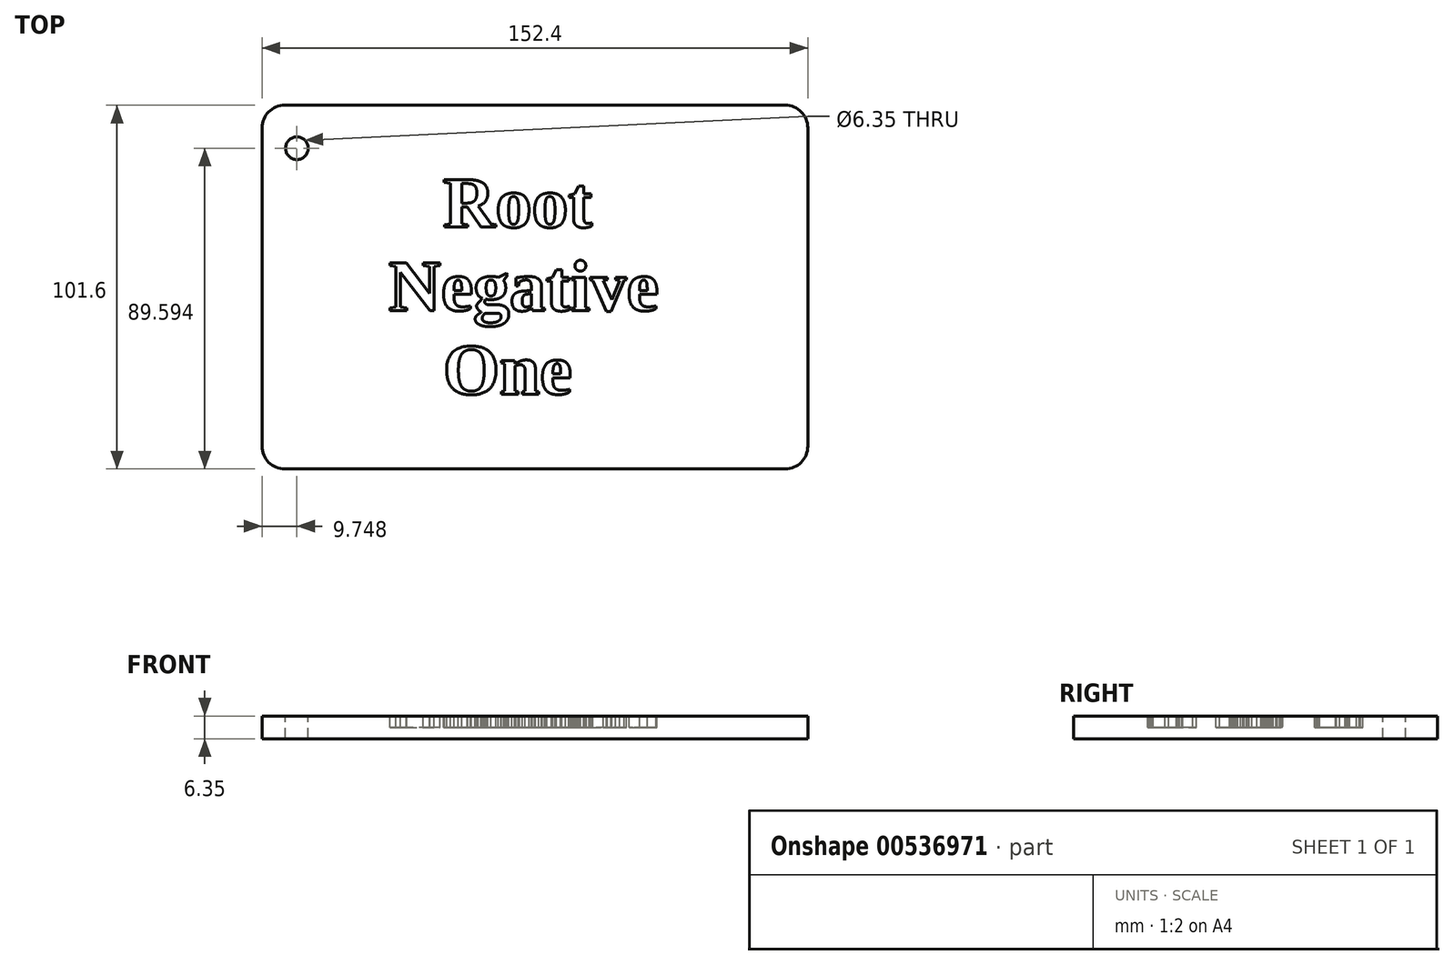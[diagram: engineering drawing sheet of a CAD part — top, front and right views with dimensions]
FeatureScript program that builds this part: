
annotation { "Feature Type Name" : "Feature", "Feature Type Description" : "" }
export const myFeature = defineFeature(function(context is Context, id is Id, definition is map)
    precondition{}
    {
        {
            var Q0;
            Q0=qCreatedBy(makeId("Top.planeOp"),FACE);
            var sketch = newSketch(context, id + "F0", { "sketchPlane" : qUnion([Q0])});
            skLineSegment(sketch, "E0.bottom", {"start": v(-67.09, 43.12) * mm, "end": v(72.61, 43.12) * mm});
            skLineSegment(sketch, "E0.top", {"start": v(-67.09, -58.48) * mm, "end": v(72.61, -58.48) * mm});
            skLineSegment(sketch, "E0.left", {"start": v(-73.44, 36.77) * mm, "end": v(-73.44, -52.13) * mm});
            skLineSegment(sketch, "E0.right", {"start": v(78.96, 36.77) * mm, "end": v(78.96, -52.13) * mm});
            skPoint(sketch, "E1.visualSharp", {"position": v(78.96, 43.12) * mm});
            skArc(sketch, "E1.filletArc", {"start": v(78.96, 36.77) * mm, "mid": v(77.1, 41.26) * mm, "end": v(72.61, 43.12) * mm});
            skPoint(sketch, "E2.visualSharp", {"position": v(78.96, -58.48) * mm});
            skArc(sketch, "E2.filletArc", {"start": v(72.61, -58.48) * mm, "mid": v(77.1, -56.62) * mm, "end": v(78.96, -52.13) * mm});
            skPoint(sketch, "E3.visualSharp", {"position": v(-73.44, -58.48) * mm});
            skArc(sketch, "E3.filletArc", {"start": v(-73.44, -52.13) * mm, "mid": v(-71.58, -56.62) * mm, "end": v(-67.09, -58.48) * mm});
            skPoint(sketch, "E4.visualSharp", {"position": v(-73.44, 43.12) * mm});
            skArc(sketch, "E4.filletArc", {"start": v(-67.09, 43.12) * mm, "mid": v(-71.58, 41.26) * mm, "end": v(-73.44, 36.77) * mm});
            skSolve(sketch);
        }
        {
            var Q0;
            Q0=makeQuery(id+"F0.imprint","IMPRINT",FACE,{"disambiguationData":[TD([[makeQuery(id+"F0.imprint","IMPRINT",EDGE,{"derivedFrom":sQuery(id+"F0.wireOp",EDGE,"E0.bottom")}),-1.0]])]});
            extrude(context, id + "F1", {"entities" : qUnion([Q0]), "depth" : 6.35 * mm, "offsetDistance" : 25.4 * mm});
        }
        {
            var Q0;
            Q0=makeQuery(id+"F1.opExtrude","CAP_FACE",FACE,{"disambiguationData":[OSD([sQuery(id+"F0.wireOp",EDGE,"E0.bottom"),sQuery(id+"F0.wireOp",EDGE,"E0.top"),sQuery(id+"F0.wireOp",EDGE,"E0.left"),sQuery(id+"F0.wireOp",EDGE,"E0.right")])],"isStart":false});
            var sketch = newSketch(context, id + "F2", { "sketchPlane" : qUnion([Q0])});
            skText(sketch, "E5", { "text": "   Root\nNegative\n   One", "fontName": "Tinos-Bold.ttf"});
            const initialGuessF2  = {"E5": [-0.0381, 0.00907, 1, 0, 0.0146]};
            skSetInitialGuess(sketch, initialGuessF2);
            skSolve(sketch);
        }
        {
            var Q0;
            Q0 = qSketchRegion(id + "F2", true);
            extrude(context, id + "F3", {"entities" : qUnion([Q0]), "operationType" : NewBodyOperationType.REMOVE, "oppositeDirection" : true, "depth" : 3.17 * mm, "offsetDistance" : 25.4 * mm});
        }
        {
            var Q0;
            {var subQ0=sQuery(id+"F0.wireOp",EDGE,"E0.left");var subQ1=sQuery(id+"F0.wireOp",EDGE,"E4.filletArc");var subQ2=sQuery(id+"F0.wireOp",EDGE,"E3.filletArc");var subQ3=sQuery(id+"F0.wireOp",EDGE,"E2.filletArc");var subQ4=sQuery(id+"F0.wireOp",EDGE,"E1.filletArc");var subQ5=sQuery(id+"F0.wireOp",EDGE,"E0.bottom");var subQ6=sQuery(id+"F0.wireOp",EDGE,"E0.right");var subQ7=sQuery(id+"F0.wireOp",EDGE,"E0.top");Q0=makeQuery(id+"F3.boolean.opBoolean","SPLIT",FACE,{"disambiguationData":[TD([makeQuery(id+"F1.opExtrude","SWEPT_FACE",FACE,{"disambiguationData":[OSD([subQ5])]})])],"derivedFrom":makeQuery(id+"F1.opExtrude","CAP_FACE",FACE,{"disambiguationData":[OSD([subQ5,subQ7,subQ0,subQ6,subQ4,subQ3,subQ2,subQ1])],"isStart":false})});}
            var sketch = newSketch(context, id + "F4", { "sketchPlane" : qUnion([Q0])});
            skCircle(sketch, "E6", {"center": v(-63.7, 31.11) * mm, "radius": 3.18 * mm});
            skSolve(sketch);
        }
        {
            var Q0;
            Q0 = qSketchRegion(id + "F4", true);
            extrude(context, id + "F5", {"entities" : qUnion([Q0]), "operationType" : NewBodyOperationType.REMOVE, "oppositeDirection" : true, "depth" : 6.35 * mm, "offsetDistance" : 25.4 * mm});
        }
    });
